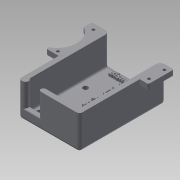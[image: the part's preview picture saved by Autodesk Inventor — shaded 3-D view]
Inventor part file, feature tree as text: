
AUTODESK INVENTOR PART (.ipt)
format: ipt  version: 2015 SP1 (Build 190203100, 203)  size: 1,158,144 bytes
history: native  units: mm
features: extrude x23, sketch x23, projected_geometry x15, fillet x10, reference x2
ambient origin geometry x8: Origin, YZ Plane, XZ Plane, XY Plane, X Axis, Y Axis, Z Axis, Center Point
bodies: Solid1 (feature_tree)
feature tree (73):
  extrude  "Extrusion1"  Depth=60.0mm
  extrude  "Extrusion3"  Depth=3.5mm TaperAngle=0.0deg
  extrude  "Extrusion4"  Depth=3.5mm TaperAngle=0.0deg
  extrude  "Extrusion5"  Depth=3.5mm TaperAngle=0.0deg
  extrude  "Extrusion6"  Depth=6.0mm
  extrude  "Extrusion7"  Depth=2.0mm
  extrude  "Extrusion8"  Depth=2.0mm
  fillet  "Fillet1"  Radius=2.0mm
  extrude  "Extrusion9"  Depth=3.5mm TaperAngle=0.0deg
  extrude  "Extrusion10"  Depth=3.5mm TaperAngle=0.0deg
  fillet  "Fillet2"  Radius=3.5mm
  extrude  "Extrusion11"  Depth=3.5mm TaperAngle=0.0deg
  extrude  "Extrusion12"  Depth=3.5mm TaperAngle=0.0deg
  extrude  "Extrusion13"  Depth=3.5mm
  extrude  "Extrusion14"  Depth=3.5mm
  sketch  "Sketch19"  dims[d76=3.5mm d77=3.5mm]
  fillet  "Fillet3"  Radius=3.5mm
  extrude  "Extrusion16"  Depth=3.5mm
  extrude  "Extrusion17"  Depth=12.5mm
  extrude  "Extrusion18"  Depth=3.5mm TaperAngle=0.0deg
  extrude  "Extrusion19"  Depth=3.5mm TaperAngle=0.0deg
  fillet  "Fillet5"  Radius=2.0mm
  fillet  "Fillet6"  Radius=1.0mm
  fillet  "Fillet7"  Radius=2.0mm
  fillet  "Fillet8"  Radius=1.0mm
  fillet  "Fillet9"  Radius=1.0mm
  fillet  "Fillet10"  Radius=1.0mm
  extrude  "Extrusion20"  Depth=3.5mm TaperAngle=0.0deg
  extrude  "Extrusion21"  Depth=3.5mm TaperAngle=0.0deg
  extrude  "Extrusion22"  Depth=3.0mm TaperAngle=0.0deg
  extrude  "Extrusion23"  [1 undecoded]
  fillet  "Fillet11"  [1 undecoded]
  extrude  "Extrusion24"  [1 undecoded]
  extrude  "Extrusion25"  [1 undecoded]
  sketch  "Sketch1"  dims[d0=42.5mm d1=60.0mm]
  sketch  "Sketch4"  dims[d2=3.5mm d3=0.0mm d11=20.0mm d12=0.0mm]
  sketch  "Sketch5"  dims[d13=3.5mm d14=0.0mm d15=3.5mm d16=0.0mm]
  sketch  "Sketch6"  dims[d17=3.5mm d18=0.0mm d19=3.5mm d20=0.0mm]
  sketch  "Sketch7"  dims[d21=6.0mm d22=6.0mm]
  reference  "Reference1"
  sketch  "Sketch8"  dims[d23=3.5mm d24=2.0mm]
  reference  "Reference2"
  sketch  "Sketch11"  dims[d25=2.0mm d26=2.0mm d27=2.0mm]
  projected_geometry  "Projected Loop1"
  projected_geometry  "Projected Loop2"
  projected_geometry  "Projected Loop3"
  sketch  "Sketch12"  dims[d28=3.5mm d29=3.5mm d30=0.0mm]
  sketch  "Sketch13"  dims[d31=2.0mm d32=3.5mm d33=0.0mm d34=3.5mm d35=0.0mm]
  projected_geometry  "Projected Loop4"
  projected_geometry  "Projected Loop5"
  projected_geometry  "Projected Loop6"
  projected_geometry  "Projected Loop7"
  projected_geometry  "Projected Loop8"
  sketch  "Sketch15"  dims[d36=3.0mm d51=3.5mm d52=0.0mm]
  sketch  "Sketch16"  dims[d53=3.5mm d54=0.0mm d55=3.5mm d56=0.0mm]
  sketch  "Sketch17"  dims[d57=3.5mm d58=0.0mm d70=1.25mm]
  sketch  "Sketch18"  dims[d71=11.75mm d72=16.0mm d73=3.5mm d74=0.0mm]
  sketch  "Sketch21"  dims[d78=25.0mm d79=12.5mm]
  projected_geometry  "Projected Loop10"
  sketch  "Sketch22"  dims[d80=20.0mm d81=3.5mm d82=0.0mm]
  projected_geometry  "Projected Loop11"
  sketch  "Sketch23"  dims[d92=3.5mm d93=0.0mm d94=3.5mm d95=0.0mm d96=2.0mm d97=1.0mm d98=2.0mm d99=1.0mm d100=1.0mm d101=1.0mm]
  projected_geometry  "Projected Loop12"
  sketch  "Sketch24"  dims[d102=3.5mm d103=0.0mm d104=3.5mm d105=0.0mm]
  projected_geometry  "Projected Loop13"
  projected_geometry  "Projected Loop14"
  sketch  "Sketch25"  dims[d106=3.5mm d107=0.0mm d108=12.5mm d109=0.0mm]
  sketch  "Sketch26"  dims[d110=1.0mm d111=3.0mm d112=0.0mm]
  projected_geometry  "Projected Loop15"
  sketch  "Sketch27"  dims[d113=2.0mm d114=0.0mm]
  projected_geometry  "Projected Loop16"
  sketch  "Sketch29"
  sketch  "Sketch30"
note: 4 required parameter values undecoded (feature->parameter linkage not recoverable at this tier; creation-order binding heuristic only, values carry confidence <= 0.55)
